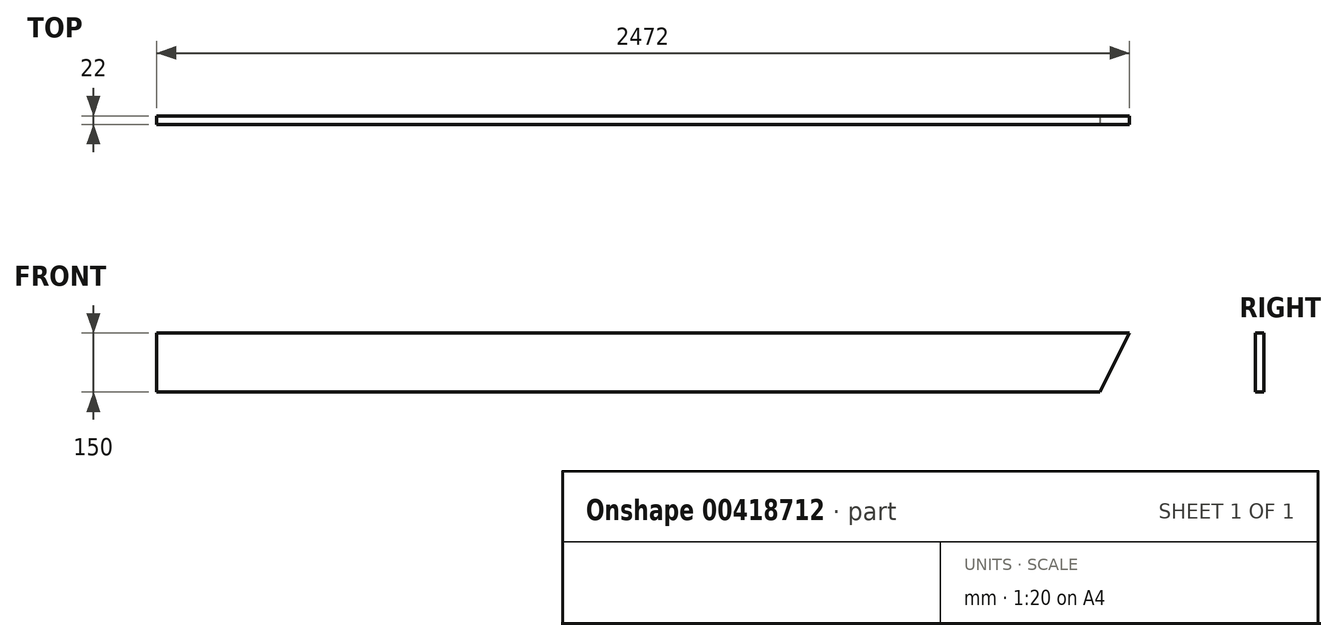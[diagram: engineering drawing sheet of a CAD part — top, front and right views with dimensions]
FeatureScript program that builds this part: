
annotation { "Feature Type Name" : "Feature", "Feature Type Description" : "" }
export const myFeature = defineFeature(function(context is Context, id is Id, definition is map)
    precondition{}
    {
        {
            var Q0;
            Q0=qCreatedBy(makeId("Right.planeOp"),FACE);
            var sketch = newSketch(context, id + "F0", { "sketchPlane" : qUnion([Q0])});
            skLineSegment(sketch, "E0.bottom", {"start": v(11, 75) * mm, "end": v(-11, 75) * mm});
            skLineSegment(sketch, "E0.top", {"start": v(11, -75) * mm, "end": v(-11, -75) * mm});
            skLineSegment(sketch, "E0.left", {"start": v(11, 75) * mm, "end": v(11, -75) * mm});
            skLineSegment(sketch, "E0.right", {"start": v(-11, 75) * mm, "end": v(-11, -75) * mm});
            skPoint(sketch, "E0.middle", {"position": v(0, 0) * mm});
            skSolve(sketch);
        }
        {
            var Q0;
            Q0=qSketchRegion(id+"F0",true);
            extrude(context, id + "F1", {"entities" : qUnion([Q0]), "oppositeDirection" : true, "depth" : (2450 + 22) * mm});
        }
        {
            var Q0;
            Q0=qCreatedBy(makeId("Front.planeOp"),FACE);
            var sketch = newSketch(context, id + "F2", { "sketchPlane" : qUnion([Q0])});
            skLineSegment(sketch, "E1", {"start": v(0, 75) * mm, "end": v(0, -75) * mm});
            skLineSegment(sketch, "E2", {"start": v(0, -75) * mm, "end": v(-75, -75) * mm});
            skLineSegment(sketch, "E3", {"start": v(-75, -75) * mm, "end": v(0, 75) * mm});
            skSolve(sketch);
        }
        {
            var Q0;
            Q0=qSketchRegion(id+"F2",true);
            extrude(context, id + "F3", {"entities" : qUnion([Q0]), "operationType" : NewBodyOperationType.REMOVE, "endBound" : BoundingType.UP_TO_NEXT, "oppositeDirection" : true, "depth" : 25 * mm, "hasSecondDirection" : true, "secondDirectionBound" : SecondDirectionBoundingType.UP_TO_NEXT, "secondDirectionOppositeDirection" : false, "secondDirectionDepth" : 25 * mm});
        }
    });
